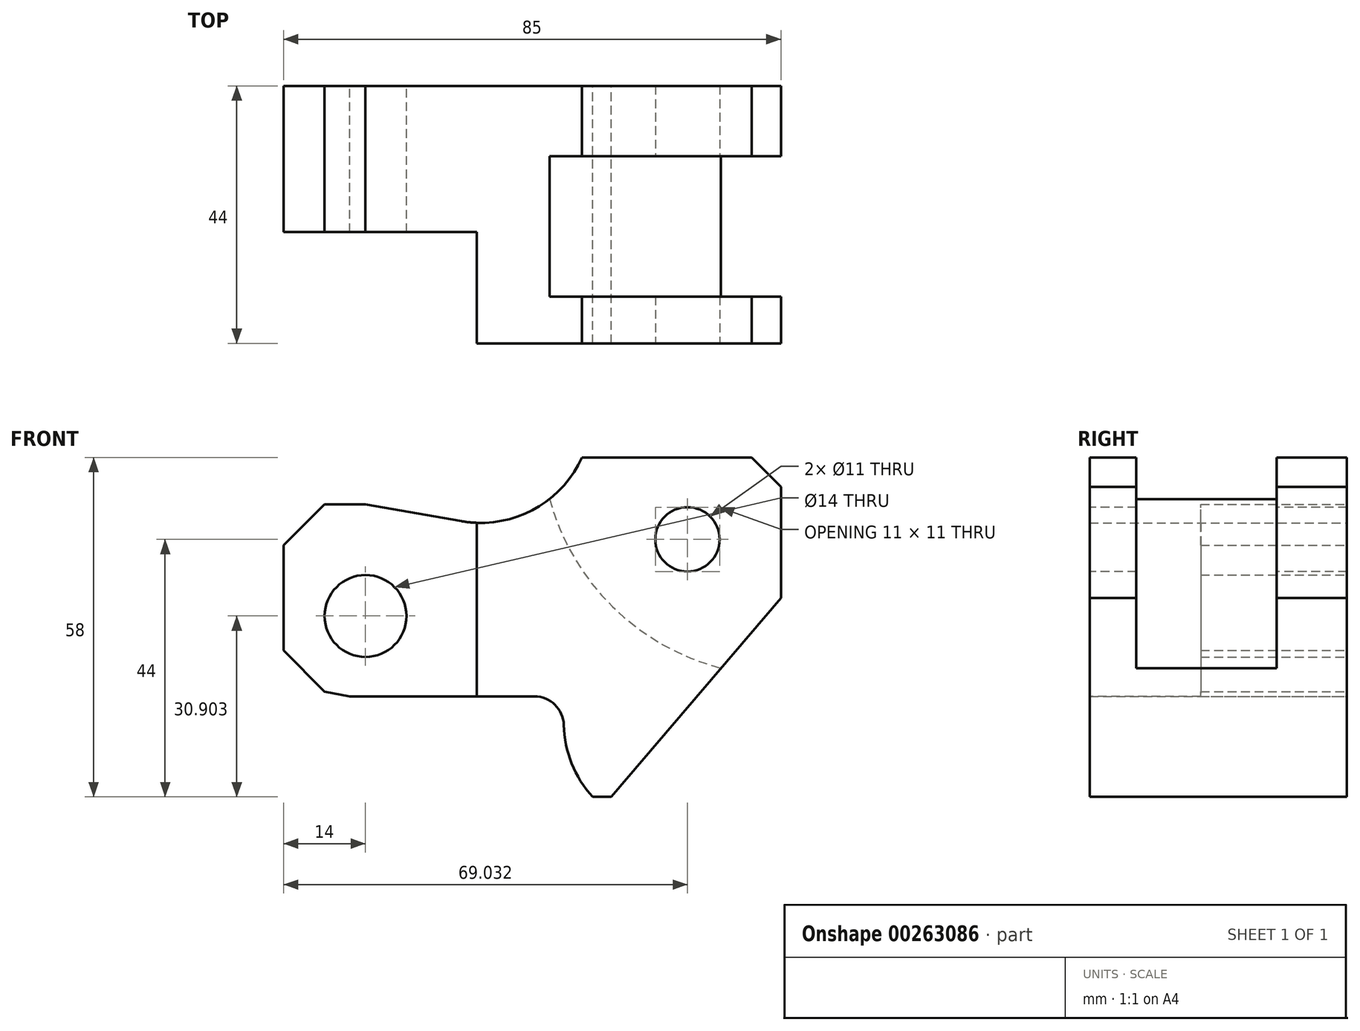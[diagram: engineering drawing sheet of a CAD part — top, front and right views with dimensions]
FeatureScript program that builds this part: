
annotation { "Feature Type Name" : "Feature", "Feature Type Description" : "" }
export const myFeature = defineFeature(function(context is Context, id is Id, definition is map)
    precondition{}
    {
        {
            var Q0;
            Q0=qCreatedBy(makeId("Front.planeOp"),FACE);
            var sketch = newSketch(context, id + "F0", { "sketchPlane" : qUnion([Q0])});
            skLineSegment(sketch, "E0", {"start": v(0, 0) * mm, "end": v(-29, -34) * mm});
            skLineSegment(sketch, "E1", {"start": v(-5, 24) * mm, "end": v(0, 19) * mm});
            skLineSegment(sketch, "E2", {"start": v(0, 19) * mm, "end": v(0, 0) * mm});
            skLineSegment(sketch, "E3", {"start": v(-34, 24) * mm, "end": v(-5, 24) * mm});
            skLineSegment(sketch, "E4", {"start": v(-78, 16) * mm, "end": v(-85, 9) * mm});
            skLineSegment(sketch, "E5", {"start": v(-78, 16) * mm, "end": v(-71, 16) * mm});
            skLineSegment(sketch, "E6", {"start": v(-85, 9) * mm, "end": v(-85, 0) * mm});
            skLineSegment(sketch, "E7", {"start": v(-78, -16) * mm, "end": v(-73.67, -16.84) * mm});
            skLineSegment(sketch, "E8", {"start": v(-85, 0) * mm, "end": v(-85, -9) * mm});
            skLineSegment(sketch, "E9", {"start": v(-78, -16) * mm, "end": v(-85, -9) * mm});
            skLineSegment(sketch, "E10", {"start": v(-71, 16) * mm, "end": v(-54.61, 13.11) * mm});
            skArc(sketch, "E11", {"start": v(-54.61, 13.11) * mm, "mid": v(-42.44, 15.02) * mm, "end": v(-34, 24) * mm});
            skLineSegment(sketch, "E12", {"start": v(-73.67, -16.84) * mm, "end": v(-71, -3.1) * mm});
            skCircle(sketch, "E13", {"center": v(-71, -3.1) * mm, "radius": 7 * mm});
            skLineSegment(sketch, "E14", {"start": v(-73.67, -16.84) * mm, "end": v(-42.11, -16.84) * mm});
            skLineSegment(sketch, "E15", {"start": v(-29, -34) * mm, "end": v(-32.2, -34) * mm});
            skArc(sketch, "E16", {"start": v(-37.11, -21.72) * mm, "mid": v(-35.76, -28.3) * mm, "end": v(-32.2, -34) * mm});
            skPoint(sketch, "E17.visualSharp", {"position": v(-36.6, -16.84) * mm});
            skArc(sketch, "E17.filletArc", {"start": v(-37.11, -21.72) * mm, "mid": v(-38.62, -18.26) * mm, "end": v(-42.11, -16.84) * mm});
            skSolve(sketch);
        }
        {
            var Q0;
            Q0=makeQuery(id+"F0.imprint","IMPRINT",FACE,{"disambiguationData":[TD([[makeQuery(id+"F0.imprint","IMPRINT",EDGE,{"derivedFrom":sQuery(id+"F0.wireOp",EDGE,"E0")}),-1.0]])]});
            extrude(context, id + "F1", {"entities" : qUnion([Q0]), "depth" : 44 * mm});
        }
        {
            var Q0;
            Q0=makeQuery(id+"F1.opExtrude","CAP_FACE",FACE,{"disambiguationData":[OSD([sQuery(id+"F0.wireOp",EDGE,"E0"),sQuery(id+"F0.wireOp",EDGE,"E1"),sQuery(id+"F0.wireOp",EDGE,"E2"),sQuery(id+"F0.wireOp",EDGE,"E3"),sQuery(id+"F0.wireOp",EDGE,"E4"),sQuery(id+"F0.wireOp",EDGE,"E5"),sQuery(id+"F0.wireOp",EDGE,"E6"),sQuery(id+"F0.wireOp",EDGE,"E7"),sQuery(id+"F0.wireOp",EDGE,"E8"),sQuery(id+"F0.wireOp",EDGE,"E9"),sQuery(id+"F0.wireOp",EDGE,"E10"),sQuery(id+"F0.wireOp",EDGE,"E11"),sQuery(id+"F0.wireOp",EDGE,"E13"),sQuery(id+"F0.wireOp",EDGE,"E14"),sQuery(id+"F0.wireOp",EDGE,"E15"),sQuery(id+"F0.wireOp",EDGE,"E16")])],"isStart":false});
            var sketch = newSketch(context, id + "F2", { "sketchPlane" : qUnion([Q0])});
            skCircle(sketch, "E18", {"center": v(-15.97, 10) * mm, "radius": 5.5 * mm});
            skSolve(sketch);
        }
        {
            var Q0;
            Q0=makeQuery(id+"F2.imprint","IMPRINT",FACE,{"disambiguationData":[TD([[makeQuery(id+"F2.imprint","IMPRINT",EDGE,{"derivedFrom":sQuery(id+"F2.wireOp",EDGE,"E18")}),1.0]])]});
            var Q1;
            Q1=sQuery(id+"F2.wireOp",EDGE,"E18");
            extrude(context, id + "F3", {"entities" : qUnion([Q0]), "operationType" : NewBodyOperationType.REMOVE, "surfaceEntities" : qUnion([Q1]), "endBound" : BoundingType.THROUGH_ALL, "oppositeDirection" : true, "depth" : 25 * mm});
        }
        {
            var Q0;
            Q0=qCreatedBy(makeId("Top.planeOp"),FACE);
            var sketch = newSketch(context, id + "F4", { "sketchPlane" : qUnion([Q0])});
            skPoint(sketch, "E19.0", {"position": v(-85, -44) * mm});
            skLineSegment(sketch, "E20.bottom", {"start": v(-85, -44) * mm, "end": v(-52, -44) * mm});
            skLineSegment(sketch, "E20.top", {"start": v(-85, -25) * mm, "end": v(-52, -25) * mm});
            skLineSegment(sketch, "E20.left", {"start": v(-85, -44) * mm, "end": v(-85, -25) * mm});
            skLineSegment(sketch, "E20.right", {"start": v(-52, -44) * mm, "end": v(-52, -25) * mm});
            skSolve(sketch);
        }
        {
            var Q0;
            Q0=qSketchRegion(id+"F4",true);
            extrude(context, id + "F5", {"entities" : qUnion([Q0]), "operationType" : NewBodyOperationType.REMOVE, "endBound" : BoundingType.THROUGH_ALL, "depth" : 25 * mm, "hasSecondDirection" : true, "secondDirectionOppositeDirection" : true, "secondDirectionDepth" : 25 * mm});
        }
        {
            var Q0;
            Q0=makeQuery(id+"F1.opExtrude","CAP_FACE",FACE,{"disambiguationData":[OSD([sQuery(id+"F0.wireOp",EDGE,"E0"),sQuery(id+"F0.wireOp",EDGE,"E1"),sQuery(id+"F0.wireOp",EDGE,"E2"),sQuery(id+"F0.wireOp",EDGE,"E3"),sQuery(id+"F0.wireOp",EDGE,"E4"),sQuery(id+"F0.wireOp",EDGE,"E5"),sQuery(id+"F0.wireOp",EDGE,"E6"),sQuery(id+"F0.wireOp",EDGE,"E7"),sQuery(id+"F0.wireOp",EDGE,"E8"),sQuery(id+"F0.wireOp",EDGE,"E9"),sQuery(id+"F0.wireOp",EDGE,"E10"),sQuery(id+"F0.wireOp",EDGE,"E11"),sQuery(id+"F0.wireOp",EDGE,"E13"),sQuery(id+"F0.wireOp",EDGE,"E14"),sQuery(id+"F0.wireOp",EDGE,"E15"),sQuery(id+"F0.wireOp",EDGE,"E16"),sQuery(id+"F0.wireOp",EDGE,"E17.filletArc")])],"isStart":true});
            cPlane(context, id + "F6", {"entities" : qUnion([Q0]), "cplaneType" : CPlaneType.OFFSET, "offset" : 12 * mm, "oppositeDirection" : true, "width" : 150 * mm, "height" : 150 * mm});
        }
        {
            var Q0;
            Q0=qCreatedBy(id+"F6.planeOp",FACE);
            var sketch = newSketch(context, id + "F7", { "sketchPlane" : qUnion([Q0])});
            skArc(sketch, "E21", {"start": v(10.24, -12) * mm, "mid": v(28.78, -1.5) * mm, "end": v(39.55, 16.9) * mm});
            skArc(sketch, "E22.0", {"start": v(52, 12.83) * mm, "mid": v(41.3, 15.68) * mm, "end": v(34, 24) * mm});
            skLineSegment(sketch, "E23.0", {"start": v(34, 24) * mm, "end": v(5, 24) * mm});
            skArc(sketch, "E24.0.0", {"start": v(34, 24) * mm, "mid": v(41.3, 15.68) * mm, "end": v(52, 12.83) * mm});
            skLineSegment(sketch, "E24.0.1", {"start": v(52, 12.83) * mm, "end": v(52, -16.84) * mm});
            skLineSegment(sketch, "E24.0.2", {"start": v(52, -16.84) * mm, "end": v(42.11, -16.84) * mm});
            skArc(sketch, "E24.0.3", {"start": v(42.11, -16.84) * mm, "mid": v(38.62, -18.26) * mm, "end": v(37.11, -21.72) * mm});
            skArc(sketch, "E24.0.4", {"start": v(37.11, -21.72) * mm, "mid": v(35.76, -28.3) * mm, "end": v(32.2, -34) * mm});
            skLineSegment(sketch, "E24.0.5", {"start": v(32.2, -34) * mm, "end": v(29, -34) * mm});
            skLineSegment(sketch, "E24.0.6", {"start": v(29, -34) * mm, "end": v(0, 0) * mm});
            skLineSegment(sketch, "E24.0.7", {"start": v(0, 0) * mm, "end": v(0, 19) * mm});
            skLineSegment(sketch, "E24.0.8", {"start": v(0, 19) * mm, "end": v(5, 24) * mm});
            skLineSegment(sketch, "E24.0.9", {"start": v(5, 24) * mm, "end": v(34, 24) * mm});
            skSolve(sketch);
        }
        {
            var Q0;
            {var subQ1=sQuery(id+"F7.wireOp",EDGE,"E21");Q0=makeQuery(id+"F7.imprint","IMPRINT",FACE,{"disambiguationData":[TD([[makeQuery(id+"F7.imprint","IMPRINT",EDGE,{"derivedFrom":subQ1}),1.0]])]});}
            extrude(context, id + "F8", {"entities" : qUnion([Q0]), "operationType" : NewBodyOperationType.REMOVE, "oppositeDirection" : true, "depth" : 24 * mm});
        }
    });
